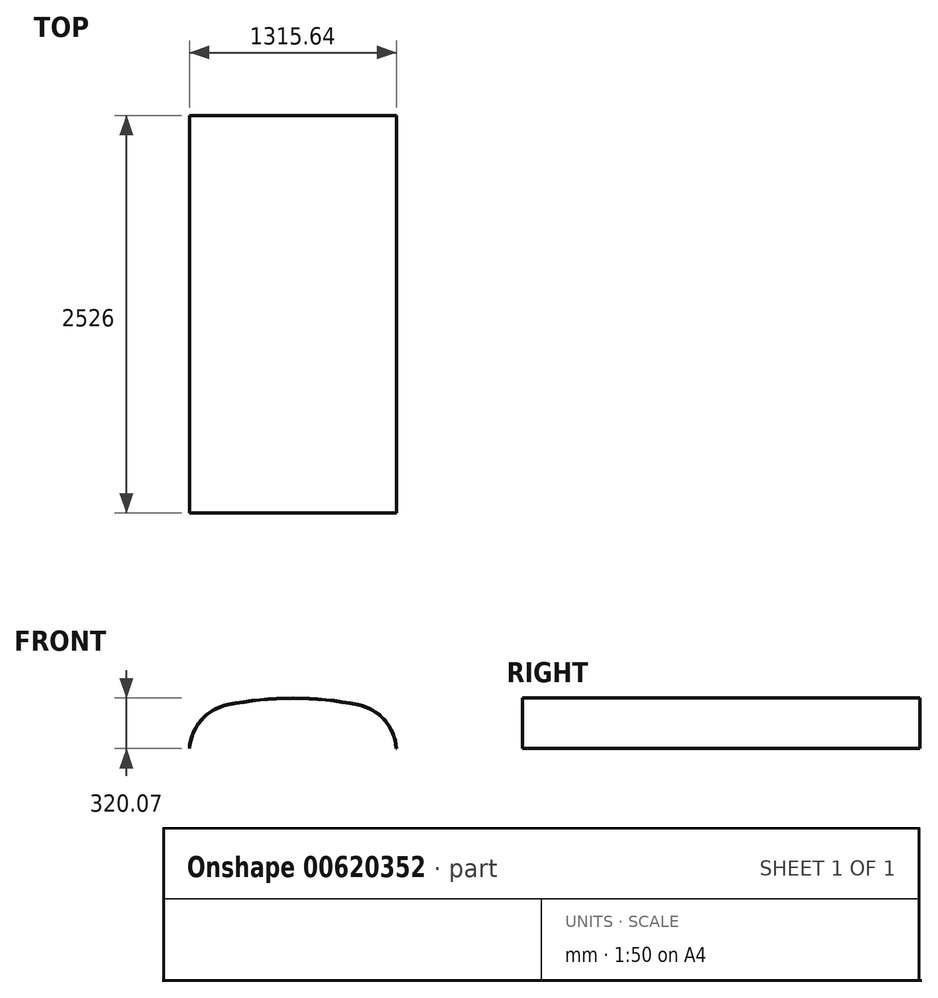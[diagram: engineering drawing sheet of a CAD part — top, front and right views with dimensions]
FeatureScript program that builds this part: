
annotation { "Feature Type Name" : "Feature", "Feature Type Description" : "" }
export const myFeature = defineFeature(function(context is Context, id is Id, definition is map)
    precondition{}
    {
        {
            var Q0;
            Q0=qCreatedBy(makeId("Front.planeOp"),FACE);
            var sketch = newSketch(context, id + "F0", { "sketchPlane" : qUnion([Q0])});
            skLineSegment(sketch, "E0", {"start": v(-685, 0) * mm, "end": v(685, 0) * mm, "construction": true});
            skLineSegment(sketch, "E1", {"start": v(-640, 1400) * mm, "end": v(640, 1400) * mm, "construction": true});
            skArc(sketch, "E2", {"start": v(414.68, 1458.6) * mm, "mid": v(0, 1500) * mm, "end": v(-414.68, 1458.6) * mm});
            skLineSegment(sketch, "E3", {"start": v(0, 1500) * mm, "end": v(0, 0) * mm, "construction": true});
            skPoint(sketch, "E3.endSnap0", {"position": v(0, 1500) * mm});
            skLineSegment(sketch, "E4", {"start": v(-685, 0) * mm, "end": v(-685, 200) * mm, "construction": true});
            skLineSegment(sketch, "E5", {"start": v(685, 0) * mm, "end": v(685, 200) * mm, "construction": true});
            skLineSegment(sketch, "E6", {"start": v(-685, 200) * mm, "end": v(685, 200) * mm, "construction": true});
            skArc(sketch, "E7", {"start": v(-654.82, 1182.93) * mm, "mid": v(-677.45, 691.7) * mm, "end": v(-685, 200) * mm, "construction": true});
            skArc(sketch, "E8", {"start": v(685, 200) * mm, "mid": v(677.45, 691.7) * mm, "end": v(654.82, 1182.93) * mm, "construction": true});
            skPoint(sketch, "E9.visualSharp", {"position": v(-640, 1400) * mm});
            skArc(sketch, "E9.filletArc", {"start": v(-414.68, 1458.6) * mm, "mid": v(-581.6, 1361.58) * mm, "end": v(-654.82, 1182.93) * mm});
            skPoint(sketch, "E10.visualSharp", {"position": v(640, 1400) * mm});
            skArc(sketch, "E10.filletArc", {"start": v(654.82, 1182.93) * mm, "mid": v(581.6, 1361.58) * mm, "end": v(414.68, 1458.6) * mm});
            skPoint(sketch, "E11", {"position": v(0, 1400) * mm});
            skArc(sketch, "E12.0", {"start": v(-415.28, 1461.55) * mm, "mid": v(-583.86, 1363.55) * mm, "end": v(-657.82, 1183.12) * mm});
            skArc(sketch, "E12.1", {"start": v(415.28, 1461.55) * mm, "mid": v(0, 1503) * mm, "end": v(-415.28, 1461.55) * mm});
            skArc(sketch, "E12.2", {"start": v(657.82, 1183.12) * mm, "mid": v(583.86, 1363.55) * mm, "end": v(415.28, 1461.55) * mm});
            skLineSegment(sketch, "E13", {"start": v(654.82, 1182.93) * mm, "end": v(657.82, 1183.12) * mm});
            skLineSegment(sketch, "E14", {"start": v(-657.82, 1183.12) * mm, "end": v(-654.82, 1182.93) * mm});
            skSolve(sketch);
        }
        {
            var Q0;
            Q0=makeQuery(id+"F0.imprint","IMPRINT",FACE,{"disambiguationData":[TD([[makeQuery(id+"F0.imprint","IMPRINT",EDGE,{"derivedFrom":sQuery(id+"F0.wireOp",EDGE,"E0")}),1.0]])]});
            var Q1;
            Q1=makeQuery(id+"F0.imprint","IMPRINT",FACE,{"disambiguationData":[TD([[makeQuery(id+"F0.imprint","IMPRINT",EDGE,{"derivedFrom":sQuery(id+"F0.wireOp",EDGE,"E2")}),-1.0]])]});
            extrude(context, id + "F1", {"entities" : qUnion([Q0, Q1]), "depth" : 2526 * mm, "offsetDistance" : 25 * mm});
        }
    });
